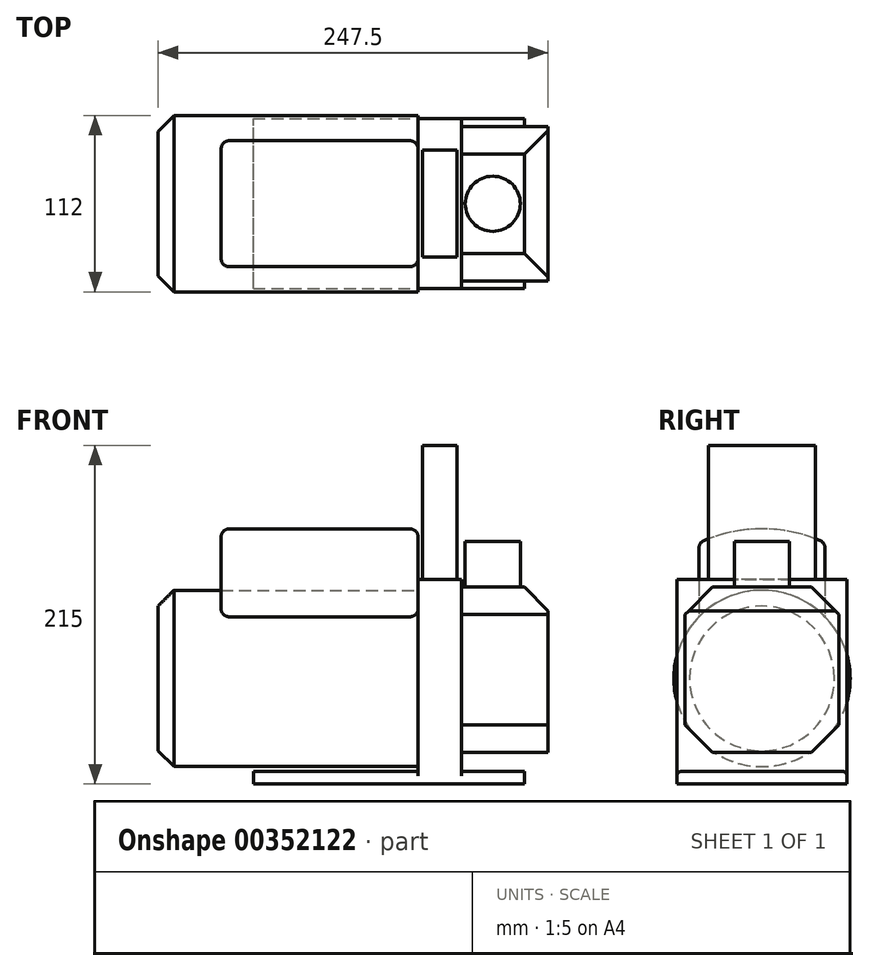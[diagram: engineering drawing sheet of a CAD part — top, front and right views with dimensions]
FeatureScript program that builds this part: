
annotation { "Feature Type Name" : "Feature", "Feature Type Description" : "" }
export const myFeature = defineFeature(function(context is Context, id is Id, definition is map)
    precondition{}
    {
        {
            var Q0;
            Q0=qCreatedBy(makeId("Top.planeOp"),FACE);
            var sketch = newSketch(context, id + "F0", { "sketchPlane" : qUnion([Q0])});
            skLineSegment(sketch, "E0.bottom", {"start": v(0, 0) * mm, "end": v(172, 0) * mm});
            skLineSegment(sketch, "E0.top", {"start": v(0, 108) * mm, "end": v(172, 108) * mm});
            skLineSegment(sketch, "E0.left", {"start": v(0, 0) * mm, "end": v(0, 108) * mm});
            skLineSegment(sketch, "E0.right", {"start": v(172, 0) * mm, "end": v(172, 108) * mm});
            skSolve(sketch);
        }
        {
            var Q0;
            Q0 = qSketchRegion(id + "F0", true);
            extrude(context, id + "F1", {"entities" : qUnion([Q0]), "depth" : 8 * mm});
        }
        {
            var Q0;
            Q0=makeQuery(id+"F1.opExtrude","CAP_FACE",FACE,{"disambiguationData":[OSD([sQuery(id+"F0.wireOp",EDGE,"E0.bottom"),sQuery(id+"F0.wireOp",EDGE,"E0.top"),sQuery(id+"F0.wireOp",EDGE,"E0.left"),sQuery(id+"F0.wireOp",EDGE,"E0.right")])],"isStart":false});
            var sketch = newSketch(context, id + "F2", { "sketchPlane" : qUnion([Q0])});
            skLineSegment(sketch, "E1.bottom", {"start": v(132, 108) * mm, "end": v(104.5, 108) * mm});
            skLineSegment(sketch, "E1.top", {"start": v(132, 0) * mm, "end": v(104.5, 0) * mm});
            skLineSegment(sketch, "E1.left", {"start": v(132, 108) * mm, "end": v(132, 0) * mm});
            skLineSegment(sketch, "E1.right", {"start": v(104.5, 108) * mm, "end": v(104.5, 0) * mm});
            skSolve(sketch);
        }
        {
            var Q0;
            Q0 = qSketchRegion(id + "F2", true);
            extrude(context, id + "F3", {"entities" : qUnion([Q0]), "operationType" : NewBodyOperationType.ADD, "depth" : 122 * mm});
        }
        {
            var Q0;
            {var subQ0=sQuery(id+"F0.wireOp",EDGE,"E0.left");var subQ1=sQuery(id+"F0.wireOp",EDGE,"E0.bottom");Q0=makeQuery(id+"F3.boolean.opBoolean","SPLIT",EDGE,{"disambiguationData":[TD([makeQuery(id+"F1.opExtrude","SWEPT_FACE",FACE,{"disambiguationData":[OSD([subQ0])]})])],"derivedFrom":makeQuery(id+"F1.opExtrude","CAP_EDGE",EDGE,{"disambiguationData":[OSD([subQ1])],"isStart":false})});}
            var Q1;
            {var subQ0=sQuery(id+"F0.wireOp",EDGE,"E0.left");var subQ1=sQuery(id+"F0.wireOp",EDGE,"E0.top");Q1=makeQuery(id+"F3.boolean.opBoolean","SPLIT",EDGE,{"disambiguationData":[TD([makeQuery(id+"F1.opExtrude","SWEPT_FACE",FACE,{"disambiguationData":[OSD([subQ0])]})])],"derivedFrom":makeQuery(id+"F1.opExtrude","CAP_EDGE",EDGE,{"disambiguationData":[OSD([subQ1])],"isStart":false})});}
            var Q2;
            {var subQ0=sQuery(id+"F0.wireOp",EDGE,"E0.right");var subQ1=sQuery(id+"F0.wireOp",EDGE,"E0.top");Q2=makeQuery(id+"F3.boolean.opBoolean","SPLIT",EDGE,{"disambiguationData":[TD([makeQuery(id+"F1.opExtrude","SWEPT_FACE",FACE,{"disambiguationData":[OSD([subQ0])]})])],"derivedFrom":makeQuery(id+"F1.opExtrude","CAP_EDGE",EDGE,{"disambiguationData":[OSD([subQ1])],"isStart":false})});}
            var Q3;
            {var subQ0=sQuery(id+"F0.wireOp",EDGE,"E0.right");var subQ1=sQuery(id+"F0.wireOp",EDGE,"E0.bottom");Q3=makeQuery(id+"F3.boolean.opBoolean","SPLIT",EDGE,{"disambiguationData":[TD([makeQuery(id+"F1.opExtrude","SWEPT_FACE",FACE,{"disambiguationData":[OSD([subQ0])]})])],"derivedFrom":makeQuery(id+"F1.opExtrude","CAP_EDGE",EDGE,{"disambiguationData":[OSD([subQ1])],"isStart":false})});}
            fillet(context, id + "F4", {"entities" : qUnion([Q0, Q1, Q2, Q3]), "radius" : 3 * mm, "tangentPropagation" : true, "allowEdgeOverflow" : false});
        }
        {
            var Q0;
            Q0=makeQuery(id+"F3.opExtrude","SWEPT_FACE",FACE,{"disambiguationData":[OSD([sQuery(id+"F2.wireOp",EDGE,"E1.left")])]});
            var sketch = newSketch(context, id + "F5", { "sketchPlane" : qUnion([Q0])});
            skLineSegment(sketch, "E2", {"start": v(85.5, 20) * mm, "end": v(22.5, 20) * mm});
            skLineSegment(sketch, "E3", {"start": v(22.5, 20) * mm, "end": v(5, 37.5) * mm});
            skLineSegment(sketch, "E4", {"start": v(5, 37.5) * mm, "end": v(5, 107.5) * mm});
            skLineSegment(sketch, "E5", {"start": v(5, 107.5) * mm, "end": v(22.5, 125) * mm});
            skLineSegment(sketch, "E6", {"start": v(22.5, 125) * mm, "end": v(85.5, 125) * mm});
            skLineSegment(sketch, "E7", {"start": v(85.5, 125) * mm, "end": v(103, 107.5) * mm});
            skLineSegment(sketch, "E8", {"start": v(103, 107.5) * mm, "end": v(103, 37.5) * mm});
            skLineSegment(sketch, "E9", {"start": v(103, 37.5) * mm, "end": v(85.5, 20) * mm});
            skSolve(sketch);
        }
        {
            var Q0;
            Q0 = qSketchRegion(id + "F5", true);
            extrude(context, id + "F6", {"entities" : qUnion([Q0]), "operationType" : NewBodyOperationType.ADD, "depth" : 55 * mm});
        }
        {
            var Q0;
            Q0=makeQuery(id+"F6.opExtrude","CAP_EDGE",EDGE,{"disambiguationData":[OSD([sQuery(id+"F5.wireOp",EDGE,"E6")])],"isStart":false});
            chamfer(context, id + "F7", {"entities" : qUnion([Q0]), "width" : 15 * mm, "tangentPropagation" : true});
        }
        {
            var Q0;
            Q0=makeQuery(id+"F6.opExtrude","SWEPT_FACE",FACE,{"disambiguationData":[OSD([sQuery(id+"F5.wireOp",EDGE,"E6")])]});
            var sketch = newSketch(context, id + "F8", { "sketchPlane" : qUnion([Q0])});
            skCircle(sketch, "E10", {"center": v(152, 54) * mm, "radius": 17.5 * mm});
            skPoint(sketch, "E10.centerSnap0", {"position": v(152, 85.5) * mm});
            skPoint(sketch, "E10.centerSnap1", {"position": v(172, 54) * mm});
            skSolve(sketch);
        }
        {
            var Q0;
            Q0 = qSketchRegion(id + "F8", true);
            extrude(context, id + "F9", {"entities" : qUnion([Q0]), "operationType" : NewBodyOperationType.ADD, "depth" : 29 * mm});
        }
        {
            var Q0;
            Q0=makeQuery(id+"F3.opExtrude","SWEPT_FACE",FACE,{"disambiguationData":[OSD([sQuery(id+"F2.wireOp",EDGE,"E1.right")])]});
            var sketch = newSketch(context, id + "F10", { "sketchPlane" : qUnion([Q0])});
            skCircle(sketch, "E11", {"center": v(-54, 67) * mm, "radius": 56 * mm});
            skPoint(sketch, "E11.centerSnap0", {"position": v(-54, 8) * mm});
            skSolve(sketch);
        }
        {
            var Q0;
            Q0 = qSketchRegion(id + "F10", true);
            extrude(context, id + "F11", {"entities" : qUnion([Q0]), "operationType" : NewBodyOperationType.ADD, "depth" : 165 * mm});
        }
        {
            var Q0;
            Q0=makeQuery(id+"F11.opExtrude","CAP_EDGE",EDGE,{"disambiguationData":[OSD([sQuery(id+"F10.wireOp",EDGE,"E11")])],"isStart":false});
            chamfer(context, id + "F12", {"entities" : qUnion([Q0]), "width" : 10 * mm, "tangentPropagation" : true});
        }
        {
            var Q0;
            {var subQ0=sQuery(id+"F2.wireOp",EDGE,"E1.bottom");var subQ1=sQuery(id+"F2.wireOp",EDGE,"E1.right");var subQ2=sQuery(id+"F2.wireOp",EDGE,"E1.top");Q0=makeQuery(id+"F11.boolean.opBoolean","SPLIT",FACE,{"disambiguationData":[TD([makeQuery(id+"F3.opExtrude","CAP_FACE",FACE,{"disambiguationData":[OSD([subQ0,subQ2,sQuery(id+"F2.wireOp",EDGE,"E1.left"),subQ1])],"isStart":false})])],"derivedFrom":makeQuery(id+"F3.opExtrude","SWEPT_FACE",FACE,{"disambiguationData":[OSD([subQ1])]})});}
            var sketch = newSketch(context, id + "F13", { "sketchPlane" : qUnion([Q0])});
            skArc(sketch, "E12", {"start": v(-14, 153.17) * mm, "mid": v(-54, 162) * mm, "end": v(-94, 153.17) * mm});
            skLineSegment(sketch, "E13", {"start": v(-14, 153.17) * mm, "end": v(-14, 106.2) * mm});
            skLineSegment(sketch, "E14", {"start": v(-94, 153.17) * mm, "end": v(-94, 106.2) * mm});
            skArc(sketch, "E15", {"start": v(-14, 106.2) * mm, "mid": v(-54, 123) * mm, "end": v(-94, 106.2) * mm});
            skSolve(sketch);
        }
        {
            var Q0;
            Q0 = qSketchRegion(id + "F13", true);
            extrude(context, id + "F14", {"entities" : qUnion([Q0]), "depth" : 125 * mm});
        }
        {
            var Q0;
            Q0=makeQuery(id+"F14.opExtrude","SWEPT_EDGE",EDGE,{"disambiguationData":[OSD([sQuery(id+"F13.wireOp",EDGE,"E12"),sQuery(id+"F13.wireOp",EDGE,"E13")])]});
            var Q1;
            Q1=makeQuery(id+"F14.opExtrude","CAP_EDGE",EDGE,{"disambiguationData":[OSD([sQuery(id+"F13.wireOp",EDGE,"E12")])],"isStart":false});
            var Q2;
            Q2=makeQuery(id+"F14.opExtrude","CAP_EDGE",EDGE,{"disambiguationData":[OSD([sQuery(id+"F13.wireOp",EDGE,"E13")])],"isStart":false});
            var Q3;
            Q3=makeQuery(id+"F14.opExtrude","CAP_EDGE",EDGE,{"disambiguationData":[OSD([sQuery(id+"F13.wireOp",EDGE,"E14")])],"isStart":false});
            var Q4;
            Q4=makeQuery(id+"F14.opExtrude","CAP_EDGE",EDGE,{"disambiguationData":[OSD([sQuery(id+"F13.wireOp",EDGE,"E12")])],"isStart":true});
            var Q5;
            Q5=makeQuery(id+"F14.opExtrude","SWEPT_EDGE",EDGE,{"disambiguationData":[OSD([sQuery(id+"F13.wireOp",EDGE,"E12"),sQuery(id+"F13.wireOp",EDGE,"E14")])]});
            var Q6;
            Q6=makeQuery(id+"F14.opExtrude","CAP_EDGE",EDGE,{"disambiguationData":[OSD([sQuery(id+"F13.wireOp",EDGE,"E13")])],"isStart":true});
            var Q7;
            Q7=makeQuery(id+"F14.opExtrude","CAP_EDGE",EDGE,{"disambiguationData":[OSD([sQuery(id+"F13.wireOp",EDGE,"E14")])],"isStart":true});
            fillet(context, id + "F15", {"entities" : qUnion([Q0, Q1, Q2, Q3, Q4, Q5, Q6, Q7]), "radius" : 5 * mm, "tangentPropagation" : true, "allowEdgeOverflow" : false});
        }
        {
            var Q0;
            Q0=makeQuery(id+"F3.opExtrude","CAP_FACE",FACE,{"disambiguationData":[OSD([sQuery(id+"F2.wireOp",EDGE,"E1.bottom"),sQuery(id+"F2.wireOp",EDGE,"E1.top"),sQuery(id+"F2.wireOp",EDGE,"E1.left"),sQuery(id+"F2.wireOp",EDGE,"E1.right")])],"isStart":false});
            var sketch = newSketch(context, id + "F16", { "sketchPlane" : qUnion([Q0])});
            skLineSegment(sketch, "E16.bottom", {"start": v(129.25, 20) * mm, "end": v(107.25, 20) * mm});
            skLineSegment(sketch, "E16.top", {"start": v(129.25, 88) * mm, "end": v(107.25, 88) * mm});
            skLineSegment(sketch, "E16.left", {"start": v(129.25, 20) * mm, "end": v(129.25, 88) * mm});
            skLineSegment(sketch, "E16.right", {"start": v(107.25, 20) * mm, "end": v(107.25, 88) * mm});
            skPoint(sketch, "E16.middle", {"position": v(118.25, 54) * mm});
            skPoint(sketch, "E16.middle.positionSnap0", {"position": v(118.25, 108) * mm});
            skPoint(sketch, "E16.middle.positionSnap1", {"position": v(132, 54) * mm});
            skPoint(sketch, "E16.centerSnap0", {"position": v(118.25, 108) * mm});
            skPoint(sketch, "E16.centerSnap1", {"position": v(132, 54) * mm});
            skSolve(sketch);
        }
        {
            var Q0;
            Q0 = qSketchRegion(id + "F16", true);
            extrude(context, id + "F17", {"entities" : qUnion([Q0]), "operationType" : NewBodyOperationType.ADD, "depth" : 85 * mm});
        }
    });
